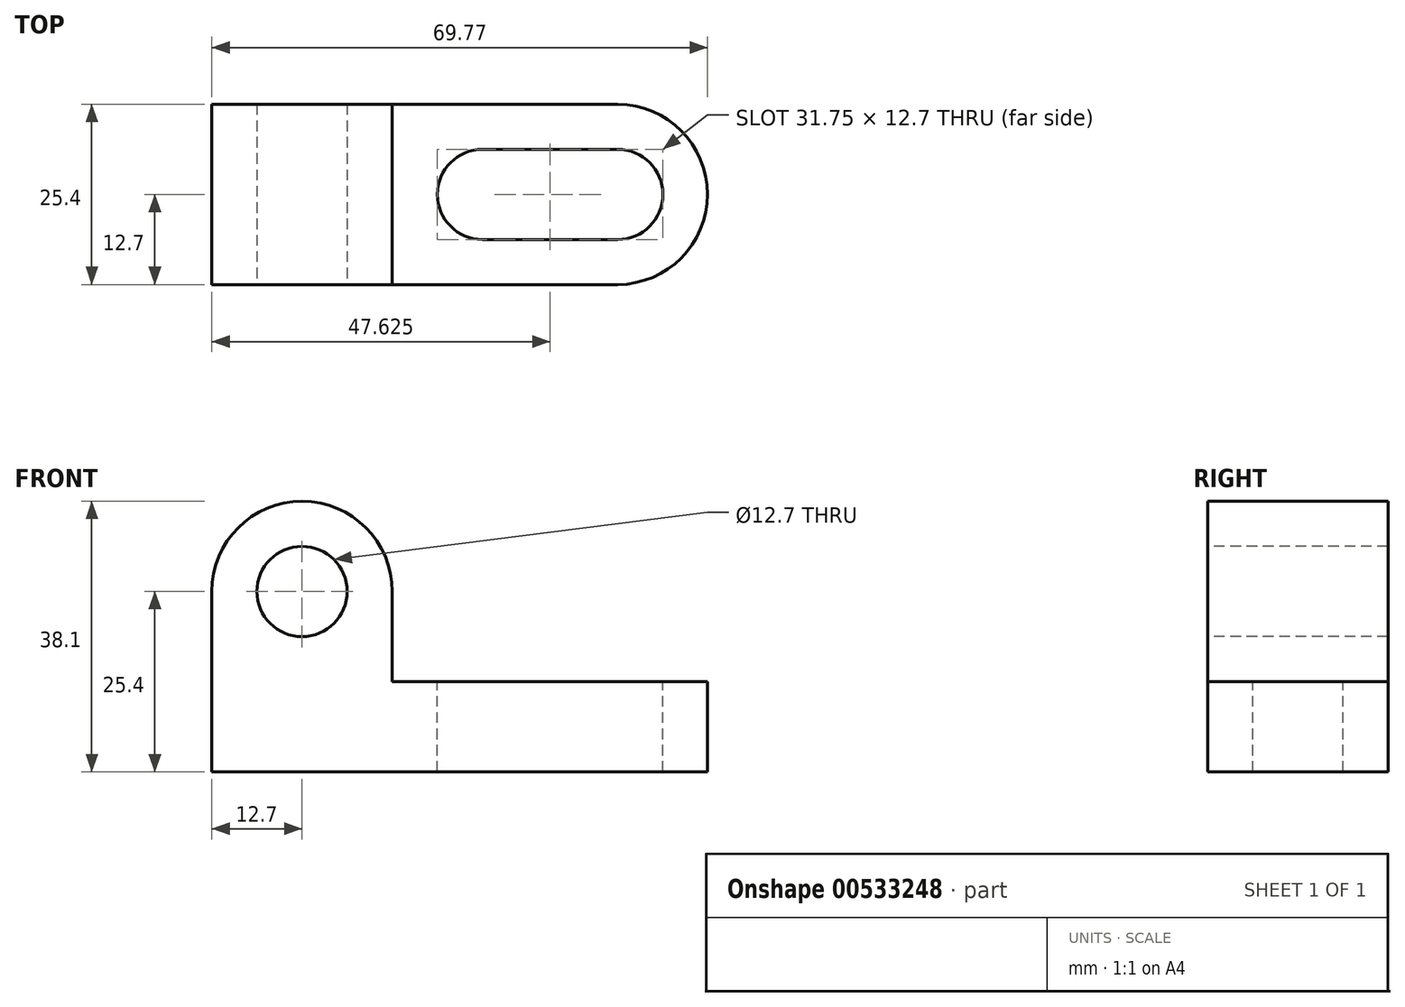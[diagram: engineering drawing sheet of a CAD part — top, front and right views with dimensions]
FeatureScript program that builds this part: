
annotation { "Feature Type Name" : "Feature", "Feature Type Description" : "" }
export const myFeature = defineFeature(function(context is Context, id is Id, definition is map)
    precondition{}
    {
        {
            var Q0;
            Q0=qCreatedBy(makeId("Front.planeOp"),FACE);
            var sketch = newSketch(context, id + "F0", { "sketchPlane" : qUnion([Q0])});
            skLineSegment(sketch, "E0.bottom", {"start": v(0, 0) * mm, "end": v(69.85, 0) * mm});
            skLineSegment(sketch, "E0.top", {"start": v(0, 38.1) * mm, "end": v(69.85, 38.1) * mm});
            skLineSegment(sketch, "E0.left", {"start": v(0, 0) * mm, "end": v(0, 38.1) * mm});
            skLineSegment(sketch, "E0.right", {"start": v(69.85, 0) * mm, "end": v(69.85, 38.1) * mm});
            skSolve(sketch);
        }
        {
            var Q0;
            Q0=makeQuery(id+"F0.imprint","IMPRINT",FACE,{"disambiguationData":[TD([[makeQuery(id+"F0.imprint","IMPRINT",EDGE,{"derivedFrom":sQuery(id+"F0.wireOp",EDGE,"E0.bottom")}),1.0]])]});
            extrude(context, id + "F1", {"entities" : qUnion([Q0]), "depth" : 25.4 * mm, "offsetDistance" : 25.4 * mm});
        }
        {
            var Q0;
            Q0=makeQuery(id+"F1.opExtrude","CAP_FACE",FACE,{"disambiguationData":[OSD([sQuery(id+"F0.wireOp",EDGE,"E0.bottom"),sQuery(id+"F0.wireOp",EDGE,"E0.top"),sQuery(id+"F0.wireOp",EDGE,"E0.left"),sQuery(id+"F0.wireOp",EDGE,"E0.right")])],"isStart":false});
            var sketch = newSketch(context, id + "F2", { "sketchPlane" : qUnion([Q0])});
            skLineSegment(sketch, "E1", {"start": v(0, 0) * mm, "end": v(0, 38.1) * mm});
            skLineSegment(sketch, "E2", {"start": v(0, 38.1) * mm, "end": v(25.4, 38.1) * mm});
            skLineSegment(sketch, "E3", {"start": v(25.4, 38.1) * mm, "end": v(25.4, 12.7) * mm});
            skLineSegment(sketch, "E4", {"start": v(25.4, 12.7) * mm, "end": v(69.85, 12.7) * mm});
            skLineSegment(sketch, "E5", {"start": v(69.85, 12.7) * mm, "end": v(69.85, 0) * mm});
            skSolve(sketch);
        }
        {
            var Q0;
            {var subQ0=sQuery(id+"F2.wireOp",EDGE,"E3");Q0=makeQuery(id+"F2.imprint","IMPRINT",FACE,{"disambiguationData":[TD([[makeQuery(id+"F2.imprint","IMPRINT",EDGE,{"derivedFrom":subQ0}),1.0]])]});}
            extrude(context, id + "F3", {"entities" : qUnion([Q0]), "operationType" : NewBodyOperationType.REMOVE, "oppositeDirection" : true, "depth" : 25.4 * mm, "offsetDistance" : 25.4 * mm});
        }
        {
            var Q0;
            Q0=makeQuery(id+"F1.opExtrude","CAP_FACE",FACE,{"disambiguationData":[OSD([sQuery(id+"F0.wireOp",EDGE,"E0.bottom"),sQuery(id+"F0.wireOp",EDGE,"E0.top"),sQuery(id+"F0.wireOp",EDGE,"E0.left"),sQuery(id+"F0.wireOp",EDGE,"E0.right")])],"isStart":false});
            var sketch = newSketch(context, id + "F4", { "sketchPlane" : qUnion([Q0])});
            skCircle(sketch, "E6", {"center": v(12.7, 25.4) * mm, "radius": 6.35 * mm});
            skArc(sketch, "E7", {"start": v(25.4, 25.4) * mm, "mid": v(12.7, 38.1) * mm, "end": v(0, 25.4) * mm});
            skSolve(sketch);
        }
        {
            var Q0;
            {var subQ0=sQuery(id+"F4.wireOp",EDGE,"E7");var subQ1=makeQuery(id+"F1.opExtrude","CAP_EDGE",EDGE,{"disambiguationData":[OSD([sQuery(id+"F0.wireOp",EDGE,"E0.left")])],"isStart":false});var subQ2=makeQuery(id+"F4.imprint","INTERSECT",VERTEX,{"derivedFrom":[subQ1,subQ0]});Q0=makeQuery(id+"F4.imprint","IMPRINT",FACE,{"disambiguationData":[TD([[makeQuery(id+"F4.imprint","IMPRINT",EDGE,{"disambiguationData":[TD([[subQ2,1.0]])],"derivedFrom":subQ0}),-1.0]])]});}
            var Q1;
            {var subQ0=sQuery(id+"F4.wireOp",EDGE,"E7");var subQ1=makeQuery(id+"F3.boolean.opBoolean","COPY",EDGE,{"derivedFrom":makeQuery(id+"F3.opExtrude","CAP_EDGE",EDGE,{"disambiguationData":[OSD([sQuery(id+"F2.wireOp",EDGE,"E3")])],"isStart":true})});var subQ2=makeQuery(id+"F4.imprint","INTERSECT",VERTEX,{"derivedFrom":[subQ1,subQ0]});Q1=makeQuery(id+"F4.imprint","IMPRINT",FACE,{"disambiguationData":[TD([[makeQuery(id+"F4.imprint","IMPRINT",EDGE,{"disambiguationData":[TD([[subQ2,-1.0]])],"derivedFrom":subQ0}),-1.0]])]});}
            var Q2;
            Q2=makeQuery(id+"F4.imprint","IMPRINT",FACE,{"disambiguationData":[TD([[makeQuery(id+"F4.imprint","IMPRINT",EDGE,{"derivedFrom":sQuery(id+"F4.wireOp",EDGE,"E6")}),1.0]])]});
            extrude(context, id + "F5", {"entities" : qUnion([Q0, Q1, Q2]), "operationType" : NewBodyOperationType.REMOVE, "oppositeDirection" : true, "depth" : 25.4 * mm, "offsetDistance" : 25.4 * mm});
        }
        {
            var Q0;
            Q0=makeQuery(id+"F3.boolean.opBoolean","COPY",FACE,{"derivedFrom":makeQuery(id+"F3.opExtrude","SWEPT_FACE",FACE,{"disambiguationData":[OSD([sQuery(id+"F2.wireOp",EDGE,"E4")])]})});
            var sketch = newSketch(context, id + "F6", { "sketchPlane" : qUnion([Q0])});
            skCircle(sketch, "E8", {"center": v(57.15, -12.7) * mm, "radius": 6.35 * mm});
            skCircle(sketch, "E9", {"center": v(38.1, -12.7) * mm, "radius": 6.35 * mm});
            skArc(sketch, "E10", {"start": v(57.15, -25.4) * mm, "mid": v(69.77, -12.7) * mm, "end": v(57.15, 0) * mm});
            skLineSegment(sketch, "E11", {"start": v(57.15, -6.35) * mm, "end": v(38.1, -6.35) * mm});
            skLineSegment(sketch, "E12", {"start": v(57.15, -19.05) * mm, "end": v(38.1, -19.05) * mm});
            skSolve(sketch);
        }
        {
            var Q0;
            {var subQ0=sQuery(id+"F6.wireOp",EDGE,"E9");var subQ1=makeQuery(id+"F6.imprint","INTERSECT",VERTEX,{"derivedFrom":[subQ0,sQuery(id+"F6.wireOp",EDGE,"E11")]});Q0=makeQuery(id+"F6.imprint","IMPRINT",FACE,{"disambiguationData":[TD([[makeQuery(id+"F6.imprint","IMPRINT",EDGE,{"disambiguationData":[TD([[subQ1,-1.0]])],"derivedFrom":subQ0}),1.0]])]});}
            var Q1;
            {var subQ0=sQuery(id+"F6.wireOp",EDGE,"E11");Q1=makeQuery(id+"F6.imprint","IMPRINT",FACE,{"disambiguationData":[TD([[makeQuery(id+"F6.imprint","IMPRINT",EDGE,{"derivedFrom":subQ0}),1.0]])]});}
            var Q2;
            {var subQ0=sQuery(id+"F6.wireOp",EDGE,"E8");var subQ1=makeQuery(id+"F6.imprint","INTERSECT",VERTEX,{"derivedFrom":[subQ0,sQuery(id+"F6.wireOp",EDGE,"E11")]});Q2=makeQuery(id+"F6.imprint","IMPRINT",FACE,{"disambiguationData":[TD([[makeQuery(id+"F6.imprint","IMPRINT",EDGE,{"disambiguationData":[TD([[subQ1,-1.0]])],"derivedFrom":subQ0}),1.0]])]});}
            var Q3;
            {var subQ0=sQuery(id+"F6.wireOp",EDGE,"E10");Q3=makeQuery(id+"F6.imprint","IMPRINT",FACE,{"disambiguationData":[TD([[makeQuery(id+"F6.imprint","IMPRINT",EDGE,{"derivedFrom":subQ0}),-1.0]])]});}
            extrude(context, id + "F7", {"entities" : qUnion([Q0, Q1, Q2, Q3]), "operationType" : NewBodyOperationType.REMOVE, "oppositeDirection" : true, "depth" : 12.7 * mm, "offsetDistance" : 25.4 * mm});
        }
    });
